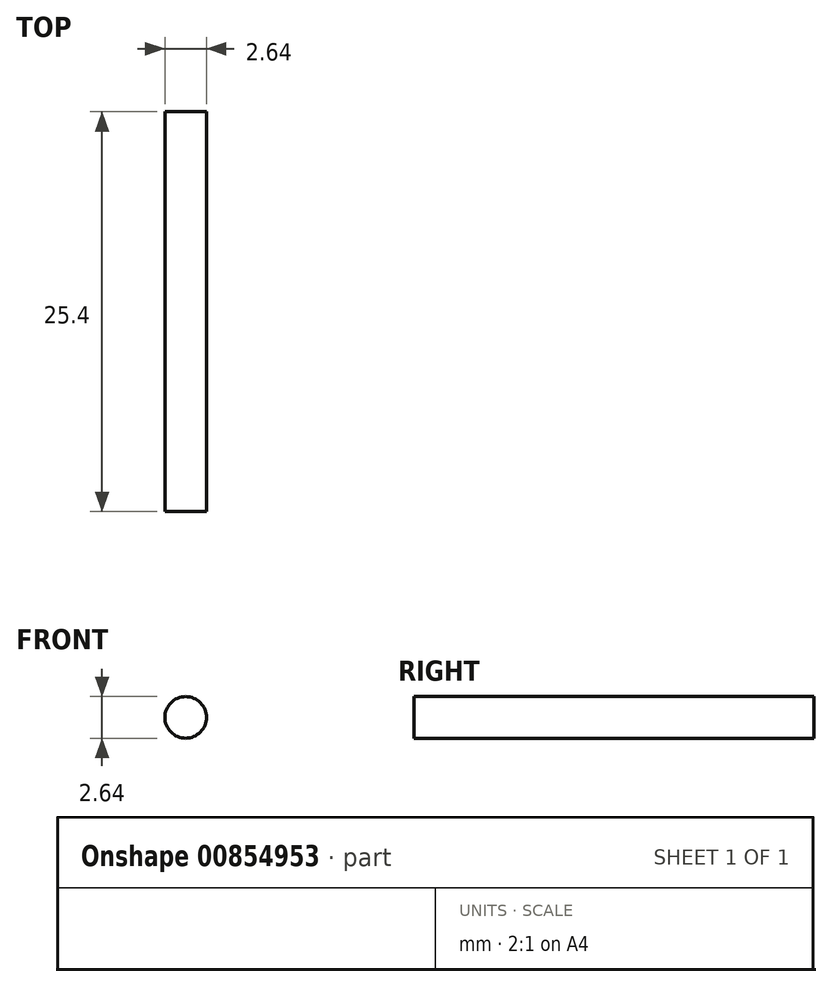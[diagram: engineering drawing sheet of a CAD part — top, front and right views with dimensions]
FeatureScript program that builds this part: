
annotation { "Feature Type Name" : "Feature", "Feature Type Description" : "" }
export const myFeature = defineFeature(function(context is Context, id is Id, definition is map)
    precondition{}
    {
        {
            var Q0;
            Q0=qCreatedBy(makeId("Front.planeOp"),FACE);
            var sketch = newSketch(context, id + "F0", { "sketchPlane" : qUnion([Q0])});
            skCircle(sketch, "E0", {"center": v(-1.32, 0) * mm, "radius": 1.32 * mm});
            skSolve(sketch);
        }
        {
            var Q0;
            Q0 = qSketchRegion(id + "F0", true);
            extrude(context, id + "F1", {"entities" : qUnion([Q0]), "depth" : 25.4 * mm, "offsetDistance" : 25.4 * mm});
        }
        {
            var Q0;
            Q0=makeQuery(id+"F1.opExtrude","CAP_FACE",FACE,{"disambiguationData":[OSD([sQuery(id+"F0.wireOp",EDGE,"E0")])],"isStart":false});
            var sketch = newSketch(context, id + "F2", { "sketchPlane" : qUnion([Q0])});
            skCircle(sketch, "E1", {"center": v(-1.32, 0) * mm, "radius": 0.8 * mm});
            skSolve(sketch);
        }
    });
